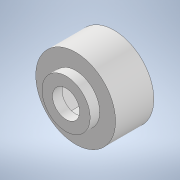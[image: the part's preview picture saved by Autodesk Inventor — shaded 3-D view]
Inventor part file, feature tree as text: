
AUTODESK INVENTOR PART (.ipt)
format: ipt  version: 2022 (Build 260153000, 153)  size: 127,488 bytes
history: native  units: in
note: dims shown in document units (in); Inventor stores cm internally (conversion verified against a paired STEP export)
features: reference x7, other x4, extrude x2, sketch x2
ambient origin geometry x8: Origin, YZ Plane, XZ Plane, XY Plane, X Axis, Y Axis, Z Axis, Center Point
bodies: Solid1 (feature_tree)
feature tree (15):
  extrude  "Extrusion1"  Depth=0.9843in
  extrude  "Extrusion2"  Depth=0.1181in
  sketch  "Sketch1"  dims[d0=0.3346in d1=0.9843in]
  reference  "Reference1"
  reference  "Reference2"
  reference  "Reference3"
  reference  "Reference4"
  reference  "Reference5"
  reference  "Reference6"
  reference  "Reference7"
  sketch  "Sketch2"  dims[d2=0.4724in d3=0.0in d4=0.3346in d5=0.1181in d6=0.0in d7=0.0197in d8=0.0344in]
  parser-record x1  (decoder bookkeeping rows leaked as tree rows — omitted from the tree; the rows remain in map.json)
  other  "model.iam"
  other  "M8 nut:2"
  other  "pivot:1"
note: 1 file-system path scrubbed to <path> (originals preserved in map.json)
